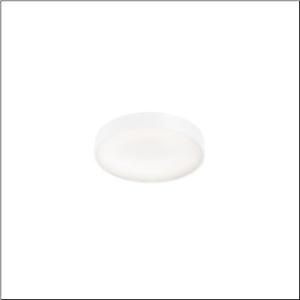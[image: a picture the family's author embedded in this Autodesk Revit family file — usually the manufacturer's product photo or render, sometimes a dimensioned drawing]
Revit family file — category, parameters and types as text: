
# Revit family: round_21_s_51mr34nd0421w
name_source: partatom
category: Lighting Fixtures
units: mm (PartAtom-declared; Revit-internal decimal feet)

## family parameters
Cut with Voids When Loaded = No
Host = Face
Light Source = No
Part Type = Normal
Room Calculation Point = No
Round Connector Dimension = Use Diameter
Shared = No

## types (1)
- Round 21 S (1 x LED, 3810 lm, 28.3 W, 4000K)
    Apparent Load = 28 VA
    CIE Flux Codes = 66 90 98 71 100
    Color Rendering = 80
    Color Temperature = 4000K
    Default Elevation = 1800 mm
    Description = Round 21 S, wall and ceiling luminaire, primary optical cover: micro prismatic cover, of PMMA, transparent, CAT 2 (L<= 3000cd/m²), light emission: direct/indirect distribution, primary light characteristic: symmetric, installation type: surface-mounted, suspended mounting, LED, rated luminous flux: 3.800lm, luminous efficacy: 135lm/W, light colour: 840, colour temperature: 4000K, control gear: DALI 2, with terminal, 5-pole, mains connection: 230V, AC, 50/60Hz, rated input power: 28.3W, housing, of aluminium, coated, white, diameter: 400mm, height: 62mm, protection rating (complete): IP40, insulation class (complete): insulation class I (protective earthing), certification: CE, impact resistance: IK04, permissible operating ambient temperature: -10..+35°C, packaging unit: 1 piece
    Height = 87 mm
    Lamp = 1 x LED
    Lamp Light Flux = 3810 lm
    Lamp Power = 28.3 W
    Lamp count = 1
    Length = 400 mm
    Luminous efficacy = 135 lm/W
    Manufacturer = Siteco
    ModVariant = No
    Model = 51MR34ND0421W
    Mounting Place = Ceiling
    Mounting Type = Surface mounted
    Number of Poles = 1
    OnlyDefault = Yes
    Power Factor = 1
    Product Name = Round 21 S
    Product group = wall and ceiling luminaire | ceiling mounted
    ProductGroupID = 304
    Protection Class = Protection class I
    Protection Degree = IP 40
    RLX_Detail_Level = 1
    RLX_Emergency_Light_Flux = 0 lm
    RLX_Emergency_Type = 0
    RLX_Emergency_Type_DB = No
    RlxData = <blob elided: 12857 chars, md5=190b873d>
    Socket = socket
    Standby Power = 0 W
    System Light Flux = 3810 lm
    System Power = 28 W
    Type Comments = Product without accessories
    Type Image = l_1258334.jpg
    URL = http://relux.com
    VarID = ---
    Voltage = 0 V
    Weight = 0.00 kg
    Width = 0 mm  [stored 0 ft]

note: [stored X ft] marks values corroborated as IEEE doubles in the binary element streams (Revit-internal decimal feet)

## geometry (parser evidence)
native form markers: Sweep x9
no freeform markers — native parametric forms only
